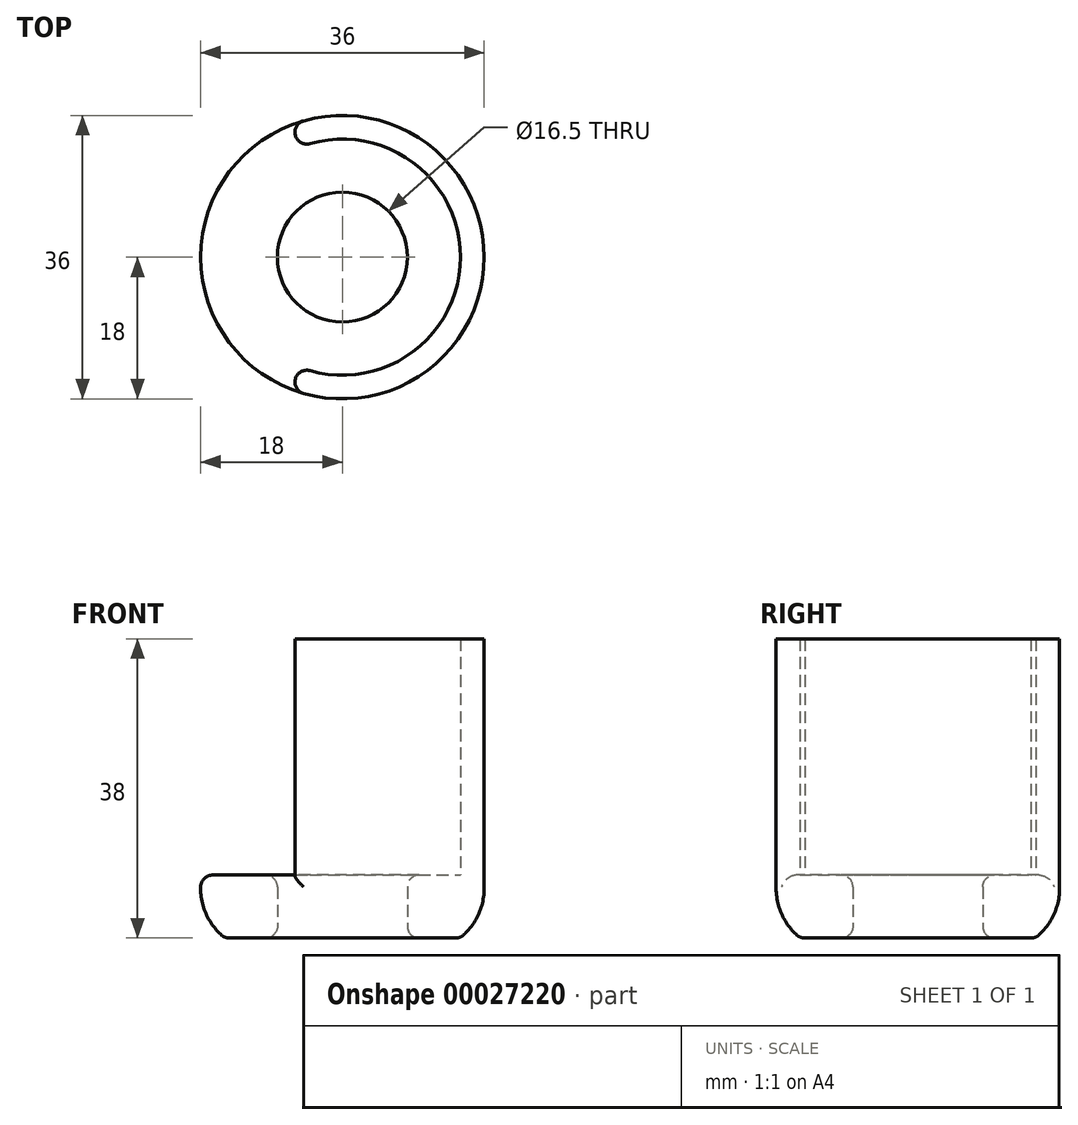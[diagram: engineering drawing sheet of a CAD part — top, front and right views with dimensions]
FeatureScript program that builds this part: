
annotation { "Feature Type Name" : "Feature", "Feature Type Description" : "" }
export const myFeature = defineFeature(function(context is Context, id is Id, definition is map)
    precondition{}
    {
        {
            var Q0;
            Q0=qCreatedBy(makeId("Top.planeOp"),FACE);
            var sketch = newSketch(context, id + "F0", { "sketchPlane" : qUnion([Q0])});
            skCircle(sketch, "E0", {"center": v(0, 0) * mm, "radius": 8.25 * mm});
            skCircle(sketch, "E1", {"center": v(0, 0) * mm, "radius": 15 * mm});
            skArc(sketch, "E2", {"start": v(-6.5, -16.79) * mm, "mid": v(18, 0) * mm, "end": v(-6.5, 16.79) * mm});
            skLineSegment(sketch, "E3", {"start": v(0, 0) * mm, "end": v(-6.5, 16.79) * mm});
            skLineSegment(sketch, "E4", {"start": v(-6.5, -16.79) * mm, "end": v(0, 0) * mm});
            skCircle(sketch, "E5", {"center": v(0, 0) * mm, "radius": 18 * mm});
            skSolve(sketch);
        }
        {
            var Q0;
            Q0=makeQuery(id+"F0.imprint","IMPRINT",FACE,{"disambiguationData":[TD([[makeQuery(id+"F0.imprint","IMPRINT",EDGE,{"derivedFrom":sQuery(id+"F0.wireOp",EDGE,"E0")}),-1.0]])]});
            extrude(context, id + "F1", {"entities" : qUnion([Q0]), "depth" : 8 * mm});
        }
        {
            var Q0;
            {var subQ3=sQuery(id+"F0.wireOp",EDGE,"E3");var subQ5=sQuery(id+"F0.wireOp",EDGE,"E1");var subQ7=makeQuery(id+"F0.imprint","INTERSECT",VERTEX,{"derivedFrom":[subQ5,subQ3]});Q0=makeQuery(id+"F0.imprint","IMPRINT",FACE,{"disambiguationData":[TD([[makeQuery(id+"F0.imprint","IMPRINT",EDGE,{"disambiguationData":[TD([[subQ7,1.0]])],"derivedFrom":subQ5}),-1.0]])]});}
            extrude(context, id + "F2", {"entities" : qUnion([Q0]), "operationType" : NewBodyOperationType.ADD, "depth" : 38 * mm});
        }
        {
            var Q0;
            {var subQ3=sQuery(id+"F0.wireOp",EDGE,"E3");var subQ5=sQuery(id+"F0.wireOp",EDGE,"E1");var subQ7=makeQuery(id+"F0.imprint","INTERSECT",VERTEX,{"derivedFrom":[subQ5,subQ3]});Q0=makeQuery(id+"F0.imprint","IMPRINT",FACE,{"disambiguationData":[TD([[makeQuery(id+"F0.imprint","IMPRINT",EDGE,{"disambiguationData":[TD([[subQ7,-1.0]])],"derivedFrom":subQ5}),-1.0]])]});}
            extrude(context, id + "F3", {"entities" : qUnion([Q0]), "operationType" : NewBodyOperationType.ADD, "depth" : 8 * mm});
        }
        {
            var Q0;
            {var subQ0=sQuery(id+"F0.wireOp",EDGE,"E5");Q0=makeQuery(id+"F3.boolean.opBoolean","MERGE",EDGE,{"derivedFrom":[makeQuery(id+"F2.opExtrude","CAP_EDGE",EDGE,{"disambiguationData":[OSD([subQ0])],"isStart":true}),makeQuery(id+"F3.opExtrude","CAP_EDGE",EDGE,{"disambiguationData":[OSD([subQ0])],"isStart":true})]});}
            chamfer(context, id + "F4", {"entities" : qUnion([Q0]), "width" : 3 * mm, "tangentPropagation" : true});
        }
        {
            var Q0;
            Q0=makeQuery(id+"F2.opExtrude","SWEPT_EDGE",EDGE,{"disambiguationData":[OSD([sQuery(id+"F0.wireOp",EDGE,"E3"),sQuery(id+"F0.wireOp",EDGE,"E5")])]});
            var Q1;
            {var subQ0=sQuery(id+"F0.wireOp",EDGE,"E1");var subQ1=sQuery(id+"F0.wireOp",EDGE,"E3");Q1=makeQuery(id+"F2.boolean.opBoolean","SPLIT",EDGE,{"disambiguationData":[TD([makeQuery(id+"F2.opExtrude","CAP_FACE",FACE,{"disambiguationData":[OSD([subQ0,subQ1,sQuery(id+"F0.wireOp",EDGE,"E4"),sQuery(id+"F0.wireOp",EDGE,"E5")])],"isStart":false})])],"derivedFrom":makeQuery(id+"F2.opExtrude","SWEPT_EDGE",EDGE,{"disambiguationData":[OSD([subQ0,subQ1])]})});}
            var Q2;
            {var subQ0=sQuery(id+"F0.wireOp",EDGE,"E1");var subQ1=sQuery(id+"F0.wireOp",EDGE,"E4");Q2=makeQuery(id+"F2.boolean.opBoolean","SPLIT",EDGE,{"disambiguationData":[TD([makeQuery(id+"F2.opExtrude","CAP_FACE",FACE,{"disambiguationData":[OSD([subQ0,sQuery(id+"F0.wireOp",EDGE,"E3"),subQ1,sQuery(id+"F0.wireOp",EDGE,"E5")])],"isStart":false})])],"derivedFrom":makeQuery(id+"F2.opExtrude","SWEPT_EDGE",EDGE,{"disambiguationData":[OSD([subQ0,subQ1])]})});}
            var Q3;
            Q3=makeQuery(id+"F2.opExtrude","SWEPT_EDGE",EDGE,{"disambiguationData":[OSD([sQuery(id+"F0.wireOp",EDGE,"E4"),sQuery(id+"F0.wireOp",EDGE,"E5")])]});
            var Q4;
            Q4=makeQuery(id+"F1.opExtrude","CAP_EDGE",EDGE,{"disambiguationData":[OSD([sQuery(id+"F0.wireOp",EDGE,"E0")])],"isStart":false});
            var Q5;
            Q5=makeQuery(id+"F3.opExtrude","CAP_EDGE",EDGE,{"disambiguationData":[OSD([sQuery(id+"F0.wireOp",EDGE,"E5")])],"isStart":false});
            var Q6;
            Q6=makeQuery(id+"F2.opExtrude","CAP_EDGE",EDGE,{"disambiguationData":[OSD([sQuery(id+"F0.wireOp",EDGE,"E5")])],"isStart":false});
            var Q7;
            Q7=makeQuery(id+"F1.opExtrude","CAP_EDGE",EDGE,{"disambiguationData":[OSD([sQuery(id+"F0.wireOp",EDGE,"E0")])],"isStart":true});
            var Q8;
            {var subQ0=sQuery(id+"F0.wireOp",EDGE,"E5");var subQ1=sQuery(id+"F0.wireOp",EDGE,"E1");var subQ2=sQuery(id+"F0.wireOp",EDGE,"E3");var subQ3=sQuery(id+"F0.wireOp",EDGE,"E4");Q8=makeQuery(id+"F4.opChamfer","BLEND_EDGE",EDGE,{"blendedFrom":[makeQuery(id+"F3.boolean.opBoolean","MERGE",EDGE,{"derivedFrom":[makeQuery(id+"F2.opExtrude","CAP_EDGE",EDGE,{"disambiguationData":[OSD([subQ0])],"isStart":true}),makeQuery(id+"F3.opExtrude","CAP_EDGE",EDGE,{"disambiguationData":[OSD([subQ0])],"isStart":true})]}),makeQuery(id+"F3.boolean.opBoolean","MERGE",FACE,{"derivedFrom":[makeQuery(id+"F2.boolean.opBoolean","MERGE",FACE,{"derivedFrom":[makeQuery(id+"F1.opExtrude","CAP_FACE",FACE,{"disambiguationData":[OSD([sQuery(id+"F0.wireOp",EDGE,"E0"),subQ1])],"isStart":true}),makeQuery(id+"F2.opExtrude","CAP_FACE",FACE,{"disambiguationData":[OSD([subQ1,subQ2,subQ3,subQ0])],"isStart":true})]}),makeQuery(id+"F3.opExtrude","CAP_FACE",FACE,{"disambiguationData":[OSD([subQ1,subQ2,subQ3,subQ0])],"isStart":true})]})],"blendedInto":[makeQuery(id+"F3.boolean.opBoolean","MERGE",FACE,{"derivedFrom":[makeQuery(id+"F2.boolean.opBoolean","MERGE",FACE,{"derivedFrom":[makeQuery(id+"F1.opExtrude","CAP_FACE",FACE,{"disambiguationData":[OSD([sQuery(id+"F0.wireOp",EDGE,"E0"),subQ1])],"isStart":true}),makeQuery(id+"F2.opExtrude","CAP_FACE",FACE,{"disambiguationData":[OSD([subQ1,subQ2,subQ3,subQ0])],"isStart":true})]}),makeQuery(id+"F3.opExtrude","CAP_FACE",FACE,{"disambiguationData":[OSD([subQ1,subQ2,subQ3,subQ0])],"isStart":true})]})]});}
            fillet(context, id + "F5", {"entities" : qUnion([Q0, Q1, Q2, Q3, Q4, Q5, Q6, Q7, Q8]), "radius" : 1.5 * mm, "tangentPropagation" : true, "allowEdgeOverflow" : false});
        }
        {
            var Q0;
            {var subQ0=sQuery(id+"F0.wireOp",EDGE,"E5");Q0=makeQuery(id+"F4.opChamfer","BLEND_EDGE",EDGE,{"blendedFrom":[makeQuery(id+"F3.boolean.opBoolean","MERGE",EDGE,{"derivedFrom":[makeQuery(id+"F2.opExtrude","CAP_EDGE",EDGE,{"disambiguationData":[OSD([subQ0])],"isStart":true}),makeQuery(id+"F3.opExtrude","CAP_EDGE",EDGE,{"disambiguationData":[OSD([subQ0])],"isStart":true})]}),makeQuery(id+"F3.boolean.opBoolean","MERGE",FACE,{"derivedFrom":[makeQuery(id+"F2.opExtrude","SWEPT_FACE",FACE,{"disambiguationData":[OSD([subQ0])]}),makeQuery(id+"F3.opExtrude","SWEPT_FACE",FACE,{"disambiguationData":[OSD([subQ0])]})]})],"blendedInto":[makeQuery(id+"F3.boolean.opBoolean","MERGE",FACE,{"derivedFrom":[makeQuery(id+"F2.opExtrude","SWEPT_FACE",FACE,{"disambiguationData":[OSD([subQ0])]}),makeQuery(id+"F3.opExtrude","SWEPT_FACE",FACE,{"disambiguationData":[OSD([subQ0])]})]})]});}
            fillet(context, id + "F6", {"entities" : qUnion([Q0]), "radius" : 8 * mm, "tangentPropagation" : true, "allowEdgeOverflow" : false});
        }
    });
